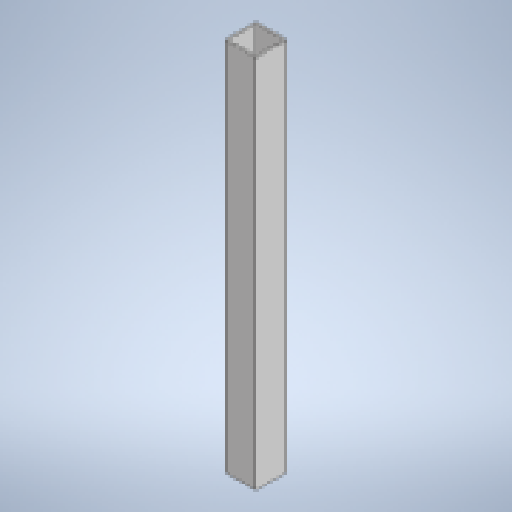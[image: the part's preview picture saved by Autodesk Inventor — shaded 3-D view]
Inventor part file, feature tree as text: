
AUTODESK INVENTOR PART (.ipt)
format: ipt  version: 2023 (Build 270158000, 158)  size: 139,776 bytes
history: native  units: in
note: dims shown in document units (in); Inventor stores cm internally (conversion verified against a paired STEP export)
features: extrude x1, sketch x1
ambient origin geometry x8: Origin, YZ Plane, XZ Plane, XY Plane, X Axis, Y Axis, Z Axis, Center Point
bodies: Solid1 (feature_tree)
feature tree (2):
  extrude  "Extrusion1"  Depth=0.0625in
  sketch  "Sketch1"  dims[d0=1.0in d1=0.0625in d2=0.0625in d3=0.0625in d4=35.4331in d5=0.0in]
